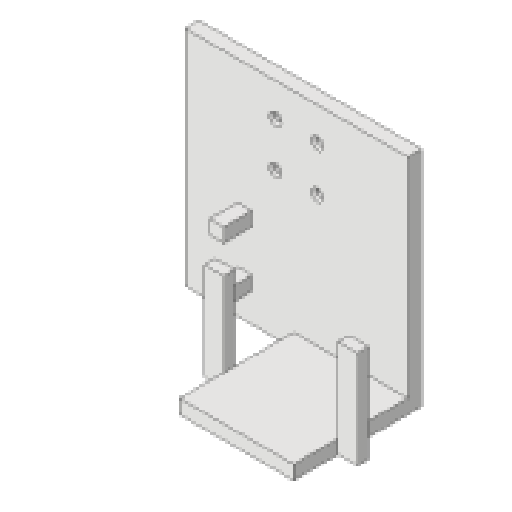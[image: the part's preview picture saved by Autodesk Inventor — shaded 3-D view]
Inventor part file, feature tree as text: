
AUTODESK INVENTOR PART (.ipt)
format: ipt  version: 2025.1 (Build 291241000, 241)  size: 189,440 bytes
history: native  units: mm
features: sketch x7, extrude x5, hole x2, other x1
ambient origin geometry x8: Origin, YZ Plane, XZ Plane, XY Plane, X Axis, Y Axis, Z Axis, Center Point
bodies: Body1 (feature_tree)
feature tree (15):
  other  "Bryła1"
  extrude  "Wyciągnięcie proste1"  Depth=80.0mm
  extrude  "Wyciągnięcie proste2"  Depth=80.0mm
  extrude  "Wyciągnięcie proste3"  Depth=5.0mm TaperAngle=0.0deg
  hole  "Otwór1"  [1 undecoded]
  extrude  "Wyciągnięcie proste4"  Depth=5.0mm
  extrude  "Wyciągnięcie proste5"  Depth=41.0mm TaperAngle=0.0deg
  hole  "Otwór2"  [1 undecoded]
  sketch  "Szkic1"
  sketch  "Szkic2"
  sketch  "Szkic3"
  sketch  "Szkic4"
  sketch  "Szkic5"
  sketch  "Szkic6"
  sketch  "Szkic10"
note: 2 required parameter values undecoded (feature->parameter linkage not recoverable at this tier; creation-order binding heuristic only, values carry confidence <= 0.55)
